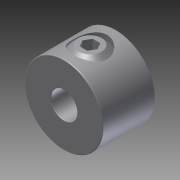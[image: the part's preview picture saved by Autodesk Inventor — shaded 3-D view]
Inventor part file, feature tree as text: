
AUTODESK INVENTOR PART (.ipt)
format: ipt  version: 2015 (Build 190159000, 159)  size: 181,248 bytes
history: native  units: in
note: dims shown in document units (in); Inventor stores cm internally (conversion verified against a paired STEP export)
features: other x2, imported_body x2, fillet x1
ambient origin geometry x8: Origin, YZ Plane, XZ Plane, XY Plane, X Axis, Y Axis, Z Axis, Center Point
bodies: Body1 (feature_tree), Body2 (feature_tree)
feature tree (5):
  fillet  "Fillet1"  [1 undecoded]
  other  "9946K4101"
  other  "Cut-Extrude2"
  imported_body  "Base1"
  imported_body  "Base2"
note: 1 required parameter value undecoded (feature->parameter linkage not recoverable at this tier; creation-order binding heuristic only, values carry confidence <= 0.55)
